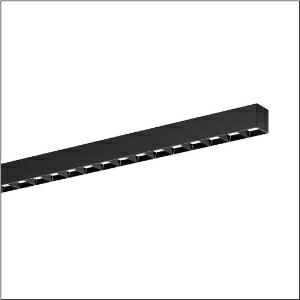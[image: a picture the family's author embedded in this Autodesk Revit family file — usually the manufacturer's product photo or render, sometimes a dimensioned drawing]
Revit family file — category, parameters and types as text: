
# Revit family: silica_r__21_51mx24tat4b_951d
name_source: partatom
category: Lighting Fixtures
units: mm (PartAtom-declared; Revit-internal decimal feet)

## family parameters
Cut with Voids When Loaded = No
Host = Face
Light Source = No
Part Type = Normal
Room Calculation Point = No
Round Connector Dimension = Use Diameter
Shared = No

## types (1)
- --- (1 x LED, 3280 lm, 32.4 W, 6500K)
    Apparent Load = 32 VA
    CIE Flux Codes = 74 94 99 100 100
    Color Rendering = 80
    Color Temperature = 6500K
    Default Elevation = 1800 mm
    Description = Silica® 21, office luminaire, primary light control with darklight reflector, of PMMA, black, light emission: direct distribution, primary light characteristic: asymmetric, installation type: surface-mounted, LED, rated luminous flux: 3.280lm, luminous efficacy: 96lm/W, light colour: 8tw, colour temperature: 2700..6500K, control gear: ECG DALI, with terminal, 3+2-pole, max. 2.5mm², mains connection: 220..240V, AC, 50/60Hz, rated input power: 34.1W, luminaire housing, of aluminium, jet black (RAL 9005), length: 1.204mm, width: 53mm, height: 53mm, protection rating (complete): IP20, insulation class (complete): insulation class I (protective earthing), certification: CE, permissible operating ambient temperature: 0..+35°C, standard: EN 50419, packaging unit: 1 piece
    Height = 0 mm  [stored 0 ft]
    Lamp = 1 x LED
    Lamp Light Flux = 3280 lm
    Lamp Power = 32.4 W
    Lamp count = 1
    Length = 1204 mm
    Luminous efficacy = 101 lm/W
    Manufacturer = Siteco
    ModVariant = No
    Model = 51MX24TAT4B
    Mounting Place = Ceiling
    Mounting Type = Recessed
    Number of Poles = 1
    OnlyDefault = Yes
    Power Factor = 1
    Product Name = Silica® 21
    Product group = office luminaire | ceiling recessed
    ProductGroupID = 400
    Protection Class = Protection class I
    Protection Degree = IP 20
    RLX_Detail_Level = 1
    RLX_Emergency_Light_Flux = 0 lm
    RLX_Emergency_Type = 0
    RLX_Emergency_Type_DB = No
    RlxData = <blob elided: 40669 chars, md5=24cead9f>
    Socket = socket
    Standby Power = 0 W
    System Light Flux = 3280 lm
    System Power = 32 W
    Type Comments = individual setting
    Type Image = l_1335908.jpg
    URL = http://relux.com
    VarID = @adj_109801
    Voltage = 0 V
    Weight = 0.00 kg
    Width = 53 mm

note: [stored X ft] marks values corroborated as IEEE doubles in the binary element streams (Revit-internal decimal feet)

## geometry (parser evidence)
native form markers: Blend x4, Sweep x10
no freeform markers — native parametric forms only
